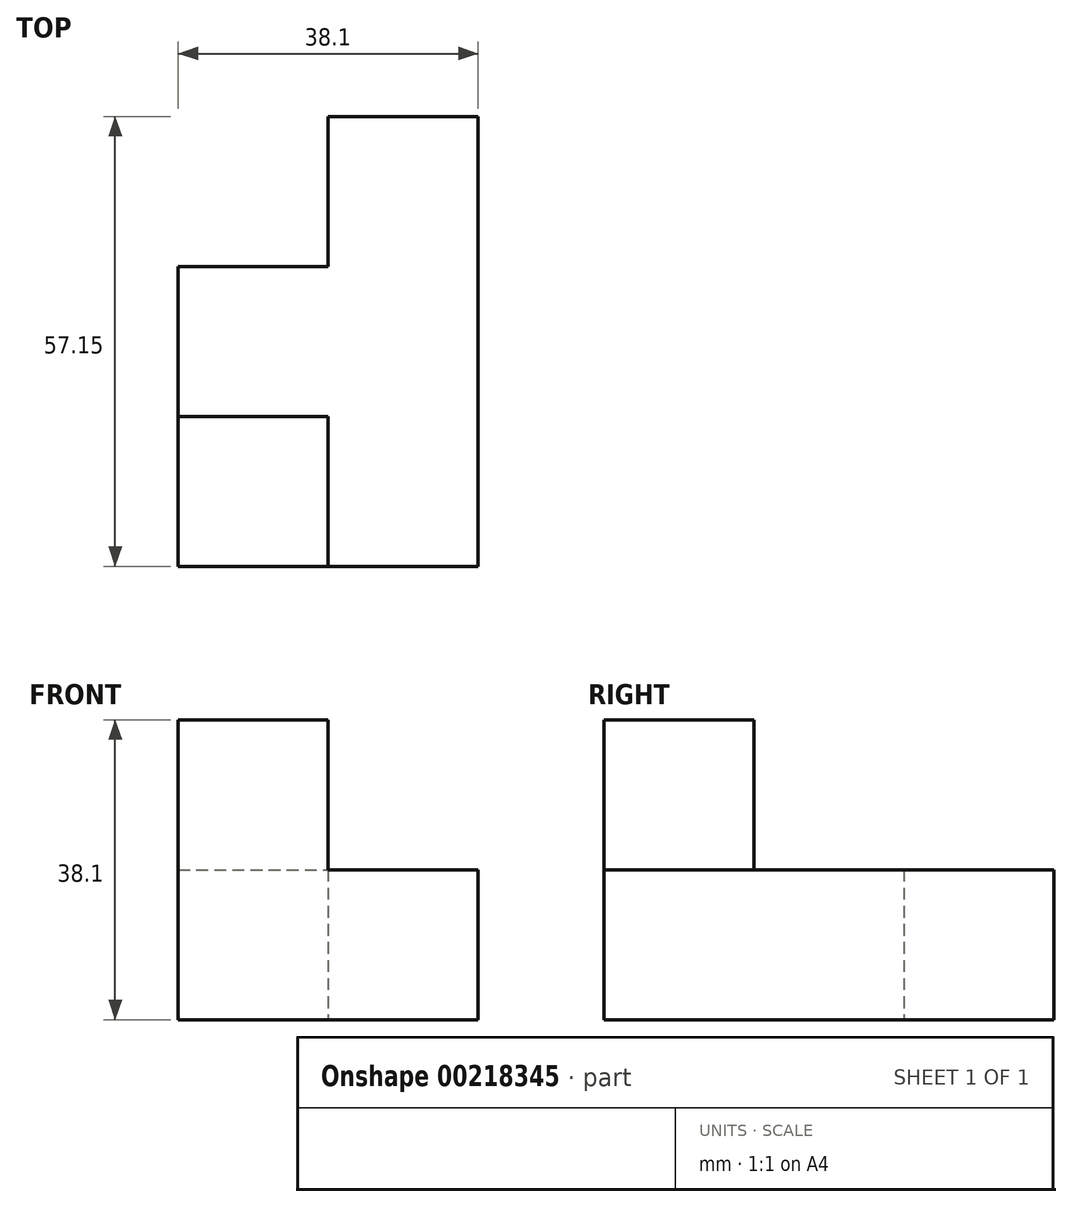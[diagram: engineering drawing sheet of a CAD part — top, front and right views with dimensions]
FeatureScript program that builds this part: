
annotation { "Feature Type Name" : "Feature", "Feature Type Description" : "" }
export const myFeature = defineFeature(function(context is Context, id is Id, definition is map)
    precondition{}
    {
        {
            var Q0;
            Q0=qCreatedBy(makeId("Front.planeOp"),FACE);
            var sketch = newSketch(context, id + "F0", { "sketchPlane" : qUnion([Q0])});
            skLineSegment(sketch, "E0.bottom", {"start": v(-7.97, 9.53) * mm, "end": v(11.08, 9.53) * mm});
            skLineSegment(sketch, "E0.top", {"start": v(-7.97, -9.53) * mm, "end": v(11.08, -9.52) * mm});
            skLineSegment(sketch, "E0.left", {"start": v(-7.97, 9.53) * mm, "end": v(-7.97, -9.53) * mm});
            skLineSegment(sketch, "E0.right", {"start": v(11.08, 9.53) * mm, "end": v(11.08, -9.53) * mm});
            skPoint(sketch, "E0.middle", {"position": v(1.55, 0) * mm});
            skSolve(sketch);
        }
        {
            var Q0;
            Q0 = qSketchRegion(id + "F0", true);
            extrude(context, id + "F1", {"entities" : qUnion([Q0]), "endBound" : BoundingType.SYMMETRIC, "depth" : 19.05 * mm});
        }
        {
            var Q0;
            Q0=makeQuery(id+"F1.opExtrude","CAP_FACE",FACE,{"disambiguationData":[OSD([sQuery(id+"F0.wireOp",EDGE,"E0.bottom"),sQuery(id+"F0.wireOp",EDGE,"E0.top"),sQuery(id+"F0.wireOp",EDGE,"E0.left"),sQuery(id+"F0.wireOp",EDGE,"E0.right")])],"isStart":false});
            extrude(context, id + "F2", {"entities" : qUnion([Q0]), "operationType" : NewBodyOperationType.ADD, "depth" : 19.05 * mm});
        }
        {
            var Q0;
            {var subQ0=sQuery(id+"F0.wireOp",EDGE,"E0.right");Q0=makeQuery(id+"F2.boolean.opBoolean","MERGE",FACE,{"derivedFrom":[makeQuery(id+"F1.opExtrude","SWEPT_FACE",FACE,{"disambiguationData":[OSD([subQ0])]}),makeQuery(id+"F2.opExtrude","SWEPT_FACE",FACE,{"disambiguationData":[OSD([subQ0])]})]});}
            extrude(context, id + "F3", {"entities" : qUnion([Q0]), "operationType" : NewBodyOperationType.ADD, "depth" : 19.05 * mm});
        }
        {
            var Q0;
            {var subQ0=sQuery(id+"F0.wireOp",EDGE,"E0.bottom");Q0=makeQuery(id+"F3.boolean.opBoolean","MERGE",FACE,{"derivedFrom":[makeQuery(id+"F2.boolean.opBoolean","MERGE",FACE,{"derivedFrom":[makeQuery(id+"F1.opExtrude","SWEPT_FACE",FACE,{"disambiguationData":[OSD([subQ0])]}),makeQuery(id+"F2.opExtrude","SWEPT_FACE",FACE,{"disambiguationData":[OSD([subQ0])]})]}),makeQuery(id+"F3.opExtrude","SWEPT_FACE",FACE,{"disambiguationData":[OSD([subQ0,sQuery(id+"F0.wireOp",EDGE,"E0.right")])]})]});}
            var sketch = newSketch(context, id + "F4", { "sketchPlane" : qUnion([Q0])});
            skLineSegment(sketch, "E1.bottom", {"start": v(-7.97, -28.58) * mm, "end": v(11.08, -28.58) * mm});
            skLineSegment(sketch, "E1.top", {"start": v(-7.97, -9.53) * mm, "end": v(11.08, -9.53) * mm});
            skLineSegment(sketch, "E1.left", {"start": v(-7.97, -28.58) * mm, "end": v(-7.97, -9.53) * mm});
            skLineSegment(sketch, "E1.right", {"start": v(11.08, -28.58) * mm, "end": v(11.08, -9.53) * mm});
            skSolve(sketch);
        }
        {
            var Q0;
            Q0=makeQuery(id+"F4.imprint","IMPRINT",FACE,{"disambiguationData":[TD([[makeQuery(id+"F4.imprint","IMPRINT",EDGE,{"derivedFrom":sQuery(id+"F4.wireOp",EDGE,"E1.bottom")}),1.0]])]});
            extrude(context, id + "F5", {"entities" : qUnion([Q0]), "operationType" : NewBodyOperationType.ADD, "depth" : 19.05 * mm});
        }
        {
            var Q0;
            {var subQ0=sQuery(id+"F0.wireOp",EDGE,"E0.right");Q0=makeQuery(id+"F3.boolean.opBoolean","MERGE",FACE,{"derivedFrom":[makeQuery(id+"F1.opExtrude","CAP_FACE",FACE,{"disambiguationData":[OSD([sQuery(id+"F0.wireOp",EDGE,"E0.bottom"),sQuery(id+"F0.wireOp",EDGE,"E0.top"),sQuery(id+"F0.wireOp",EDGE,"E0.left"),subQ0])],"isStart":true}),makeQuery(id+"F3.opExtrude","SWEPT_FACE",FACE,{"disambiguationData":[OSD([subQ0]),TDD([makeQuery(id+"F1.opExtrude","CAP_EDGE",EDGE,{"disambiguationData":[OSD([subQ0])],"isStart":true})])]})]});}
            var sketch = newSketch(context, id + "F6", { "sketchPlane" : qUnion([Q0])});
            skLineSegment(sketch, "E2.bottom", {"start": v(-30.13, 9.52) * mm, "end": v(-11.08, 9.52) * mm});
            skLineSegment(sketch, "E2.top", {"start": v(-30.13, -9.52) * mm, "end": v(-11.08, -9.52) * mm});
            skLineSegment(sketch, "E2.left", {"start": v(-30.13, 9.52) * mm, "end": v(-30.13, -9.52) * mm});
            skLineSegment(sketch, "E2.right", {"start": v(-11.08, 9.52) * mm, "end": v(-11.08, -9.52) * mm});
            skSolve(sketch);
        }
        {
            var Q0;
            Q0=makeQuery(id+"F6.imprint","IMPRINT",FACE,{"disambiguationData":[TD([[makeQuery(id+"F6.imprint","IMPRINT",EDGE,{"derivedFrom":sQuery(id+"F6.wireOp",EDGE,"E2.bottom")}),1.0]])]});
            extrude(context, id + "F7", {"entities" : qUnion([Q0]), "operationType" : NewBodyOperationType.ADD, "depth" : 19.05 * mm});
        }
    });
